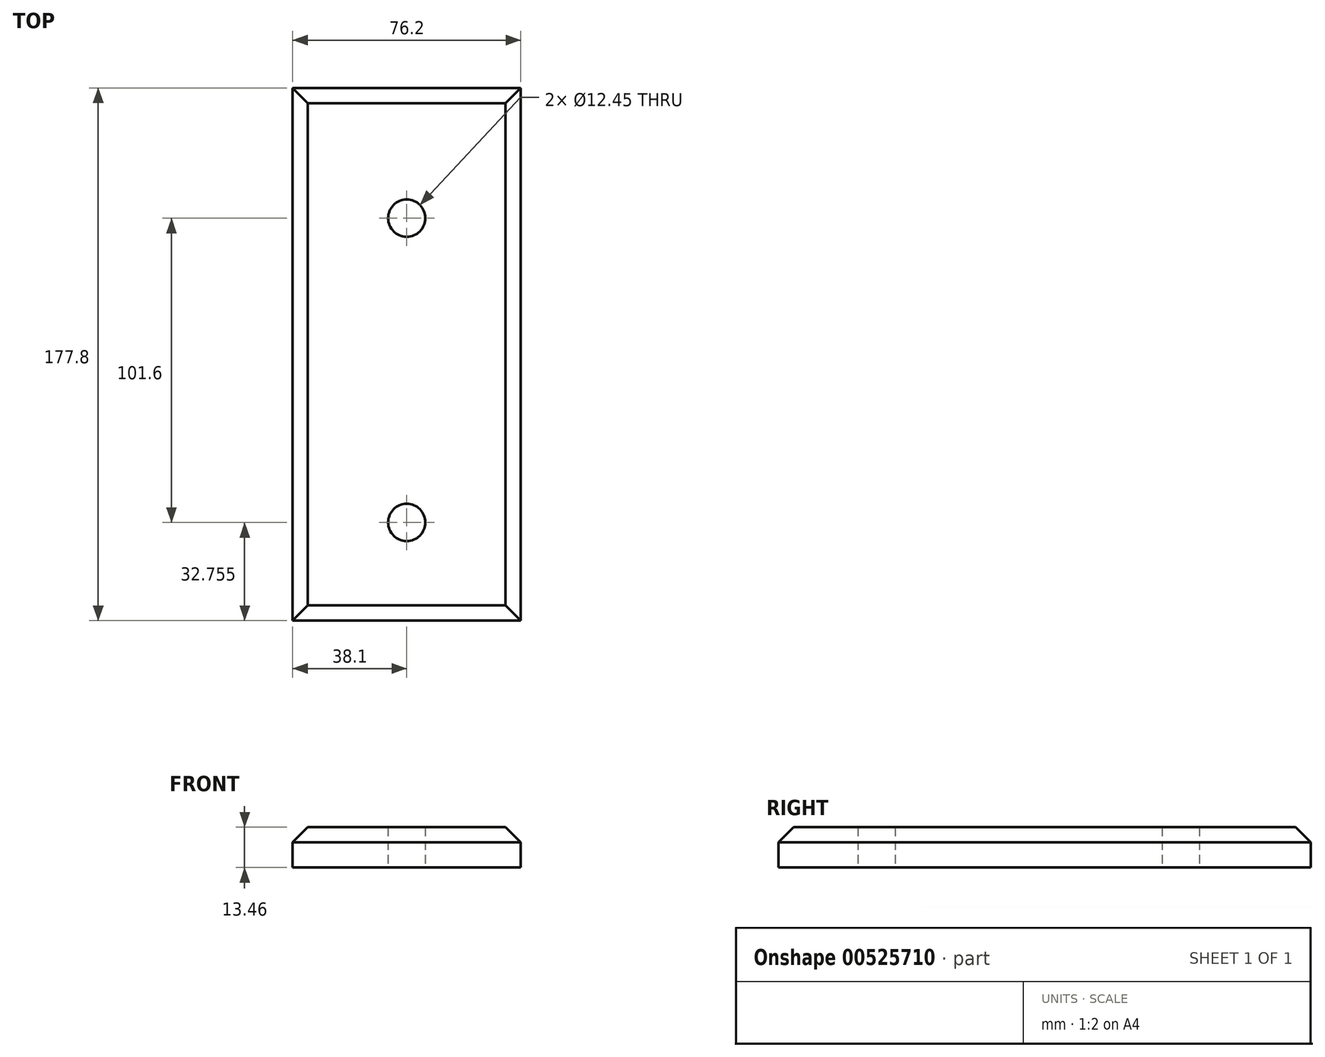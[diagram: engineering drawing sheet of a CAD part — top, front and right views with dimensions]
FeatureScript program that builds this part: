
annotation { "Feature Type Name" : "Feature", "Feature Type Description" : "" }
export const myFeature = defineFeature(function(context is Context, id is Id, definition is map)
    precondition{}
    {
        {
            var Q0;
            Q0=qCreatedBy(makeId("Top.planeOp"),FACE);
            var sketch = newSketch(context, id + "F0", { "sketchPlane" : qUnion([Q0])});
            skLineSegment(sketch, "E0.bottom", {"start": v(-38.1, 88.9) * mm, "end": v(38.1, 88.9) * mm});
            skLineSegment(sketch, "E0.top", {"start": v(-38.1, -88.9) * mm, "end": v(38.1, -88.9) * mm});
            skLineSegment(sketch, "E0.left", {"start": v(-38.1, 88.9) * mm, "end": v(-38.1, -88.9) * mm});
            skLineSegment(sketch, "E0.right", {"start": v(38.1, 88.9) * mm, "end": v(38.1, -88.9) * mm});
            skPoint(sketch, "E0.middle", {"position": v(0, 0) * mm});
            skLineSegment(sketch, "E1", {"start": v(0, 88.9) * mm, "end": v(0, -88.9) * mm});
            skCircle(sketch, "E2", {"center": v(0, -56.15) * mm, "radius": 6.22 * mm});
            skCircle(sketch, "E3", {"center": v(0, 45.45) * mm, "radius": 6.22 * mm});
            skSolve(sketch);
        }
        {
            var Q0;
            {var subQ0=sQuery(id+"F0.wireOp",EDGE,"E0.right");Q0=makeQuery(id+"F0.imprint","IMPRINT",FACE,{"disambiguationData":[TD([[makeQuery(id+"F0.imprint","IMPRINT",EDGE,{"derivedFrom":subQ0}),-1.0]])]});}
            var Q1;
            {var subQ5=sQuery(id+"F0.wireOp",EDGE,"E0.left");Q1=makeQuery(id+"F0.imprint","IMPRINT",FACE,{"disambiguationData":[TD([[makeQuery(id+"F0.imprint","IMPRINT",EDGE,{"derivedFrom":subQ5}),1.0]])]});}
            extrude(context, id + "F1", {"entities" : qUnion([Q0, Q1]), "depth" : 13.46 * mm, "offsetDistance" : 25.4 * mm});
        }
        {
            var Q0;
            Q0=makeQuery(id+"F1.opExtrude","CAP_EDGE",EDGE,{"disambiguationData":[OSD([sQuery(id+"F0.wireOp",EDGE,"E0.left")])],"isStart":false});
            var Q1;
            Q1=makeQuery(id+"F1.opExtrude","CAP_EDGE",EDGE,{"disambiguationData":[OSD([sQuery(id+"F0.wireOp",EDGE,"E0.right")])],"isStart":false});
            var Q2;
            Q2=makeQuery(id+"F1.opExtrude","CAP_EDGE",EDGE,{"disambiguationData":[OSD([sQuery(id+"F0.wireOp",EDGE,"E0.bottom")])],"isStart":false});
            var Q3;
            Q3=makeQuery(id+"F1.opExtrude","CAP_EDGE",EDGE,{"disambiguationData":[OSD([sQuery(id+"F0.wireOp",EDGE,"E0.top")])],"isStart":false});
            chamfer(context, id + "F2", {"entities" : qUnion([Q0, Q1, Q2, Q3]), "width" : 5.08 * mm, "tangentPropagation" : true});
        }
    });
